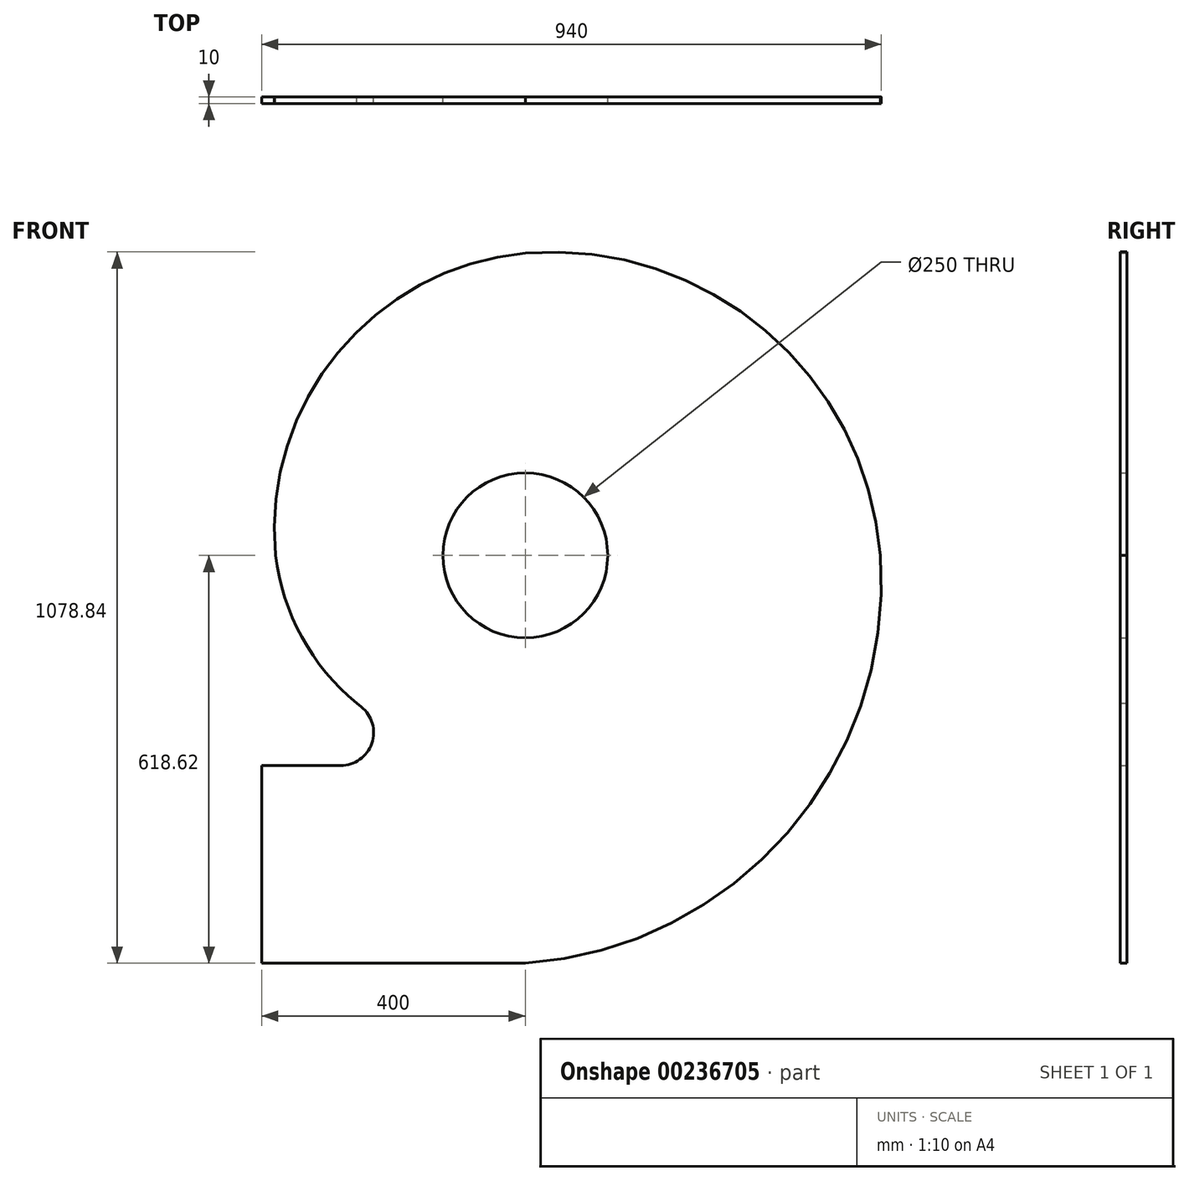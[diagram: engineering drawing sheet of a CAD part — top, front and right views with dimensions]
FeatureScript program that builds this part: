
annotation { "Feature Type Name" : "Feature", "Feature Type Description" : "" }
export const myFeature = defineFeature(function(context is Context, id is Id, definition is map)
    precondition{}
    {
        {
            var Q0;
            Q0=qCreatedBy(makeId("Front.planeOp"),FACE);
            var sketch = newSketch(context, id + "F0", { "sketchPlane" : qUnion([Q0])});
            skLineSegment(sketch, "E0", {"start": v(0, 687.71) * mm, "end": v(0, -665.24) * mm, "construction": true});
            skLineSegment(sketch, "E1", {"start": v(712.27, 0) * mm, "end": v(-772.7, 0) * mm, "construction": true});
            skLineSegment(sketch, "E2", {"start": v(-772.7, 0) * mm, "end": v(-772.7, -643.59) * mm, "construction": true});
            skLineSegment(sketch, "E3", {"start": v(-806.58, -550) * mm, "end": v(762.9, -550) * mm, "construction": true});
            skLineSegment(sketch, "E4", {"start": v(-625.97, -0.99) * mm, "end": v(-621.07, -3.81) * mm});
            skCircle(sketch, "E5", {"center": v(0, 0) * mm, "radius": 320 * mm, "construction": true});
            skLineSegment(sketch, "E6.bottom", {"start": v(-40, 40) * mm, "end": v(40, 40) * mm, "construction": true});
            skLineSegment(sketch, "E6.top", {"start": v(-40, -40) * mm, "end": v(40, -40) * mm, "construction": true});
            skLineSegment(sketch, "E6.left", {"start": v(-40, 40) * mm, "end": v(-40, -40) * mm, "construction": true});
            skLineSegment(sketch, "E6.right", {"start": v(40, 40) * mm, "end": v(40, -40) * mm, "construction": true});
            skArc(sketch, "E7", {"start": v(538.62, 0) * mm, "mid": v(375.2, -444.99) * mm, "end": v(-65.58, -619.44) * mm});
            skArc(sketch, "E8", {"start": v(538.62, 0) * mm, "mid": v(364.3, 340.86) * mm, "end": v(0, 458.62) * mm});
            skArc(sketch, "E9", {"start": v(0, 458.62) * mm, "mid": v(-284.3, 307.72) * mm, "end": v(-378.62, 0) * mm});
            skLineSegment(sketch, "E10", {"start": v(0, -618.62) * mm, "end": v(-400, -618.62) * mm});
            skLineSegment(sketch, "E11", {"start": v(-400, -618.62) * mm, "end": v(-400, -318.62) * mm});
            skLineSegment(sketch, "E12", {"start": v(-400, -318.62) * mm, "end": v(-280.02, -318.62) * mm});
            skLineSegment(sketch, "E13", {"start": v(-248.88, -229.5) * mm, "end": v(-255.85, -223.96) * mm});
            skPoint(sketch, "E14.visualSharp", {"position": v(-136.95, -318.62) * mm});
            skArc(sketch, "E14.filletArc", {"start": v(-280.02, -318.62) * mm, "mid": v(-232.82, -285.11) * mm, "end": v(-248.88, -229.5) * mm});
            skArc(sketch, "E15", {"start": v(-378.62, 0) * mm, "mid": v(-339, -123.9) * mm, "end": v(-255.85, -223.96) * mm});
            skPoint(sketch, "E15.startSnap0", {"position": v(-40, 0) * mm});
            skCircle(sketch, "E16", {"center": v(0, 0) * mm, "radius": 125 * mm});
            skSolve(sketch);
        }
        {
            var Q0;
            Q0=makeQuery(id+"F0.imprint","IMPRINT",FACE,{"disambiguationData":[TD([[makeQuery(id+"F0.imprint","IMPRINT",EDGE,{"derivedFrom":sQuery(id+"F0.wireOp",EDGE,"ZozrHHeU-78oO-nen7-godN-t5K95oYBgX9X")}),1.0]])]});
            var Q1;
            {var subQ1=sQuery(id+"F0.wireOp",EDGE,"E8");Q1=makeQuery(id+"F0.imprint","IMPRINT",FACE,{"disambiguationData":[TD([[makeQuery(id+"F0.imprint","IMPRINT",EDGE,{"derivedFrom":subQ1}),1.0]])]});}
            extrude(context, id + "F1", {"entities" : qUnion([Q0, Q1]), "depth" : 10 * mm, "offsetDistance" : 25 * mm});
        }
    });
